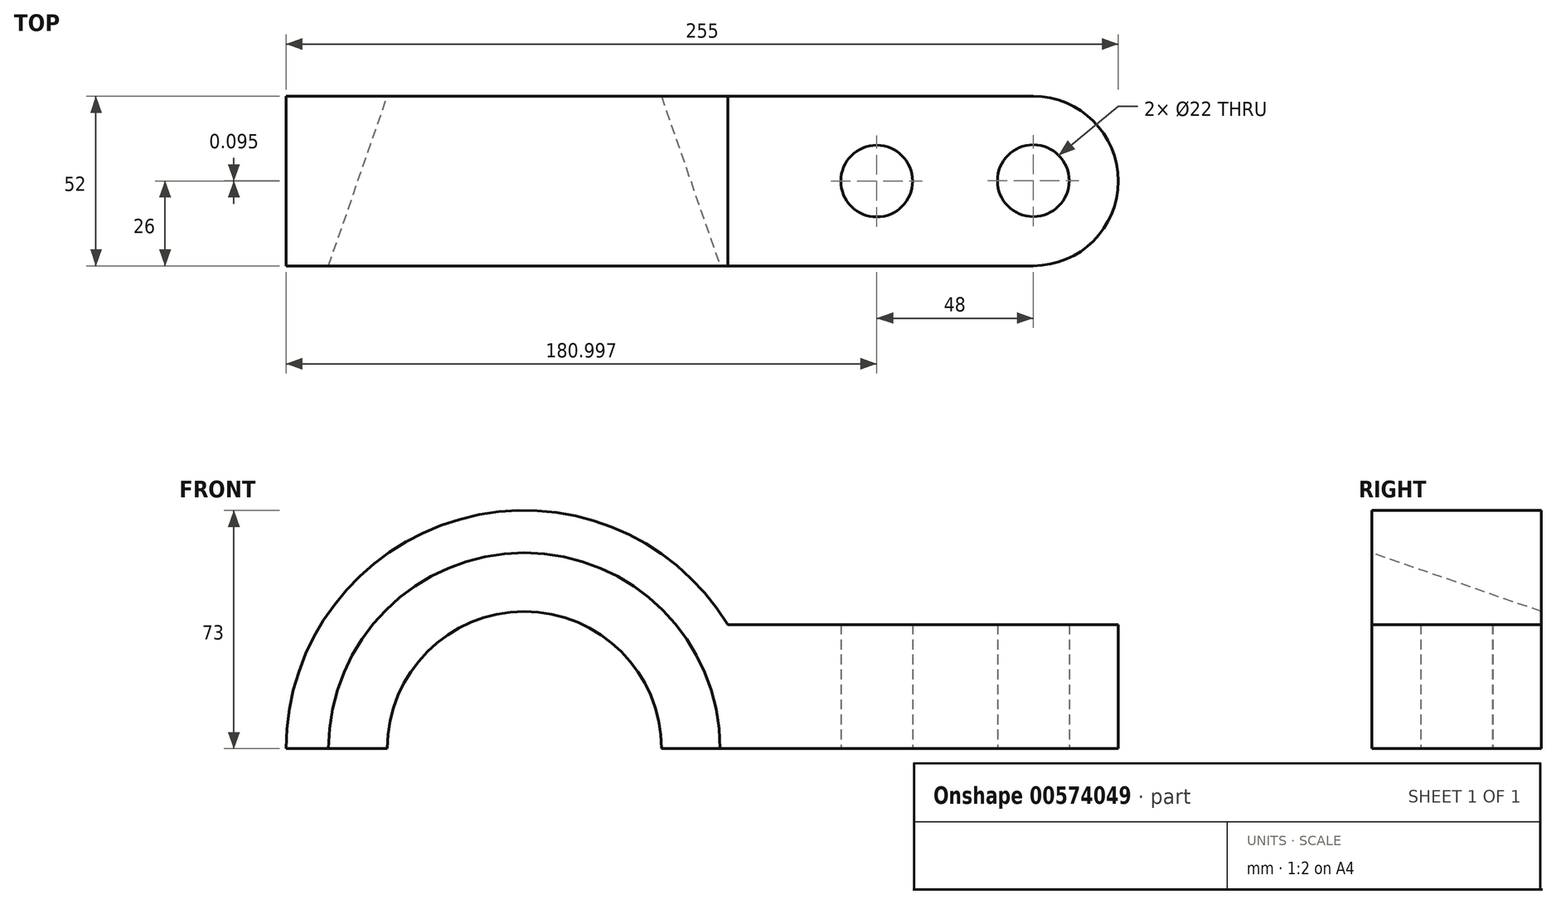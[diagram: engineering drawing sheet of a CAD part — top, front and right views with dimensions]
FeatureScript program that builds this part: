
annotation { "Feature Type Name" : "Feature", "Feature Type Description" : "" }
export const myFeature = defineFeature(function(context is Context, id is Id, definition is map)
    precondition{}
    {
        {
            var Q0;
            Q0=qCreatedBy(makeId("Front.planeOp"),FACE);
            var sketch = newSketch(context, id + "F0", { "sketchPlane" : qUnion([Q0])});
            skArc(sketch, "E0", {"start": v(-38.55, 38) * mm, "mid": v(-120.62, 70.28) * mm, "end": v(-173.88, 0) * mm});
            skArc(sketch, "E1", {"start": v(-40.88, 0) * mm, "mid": v(-100.88, 60) * mm, "end": v(-160.88, 0) * mm});
            skArc(sketch, "E2", {"start": v(-58.88, 0) * mm, "mid": v(-100.88, 42) * mm, "end": v(-142.88, 0) * mm});
            skLineSegment(sketch, "E3", {"start": v(-38.55, 38) * mm, "end": v(81.12, 38) * mm});
            skLineSegment(sketch, "E4", {"start": v(81.12, 38) * mm, "end": v(81.12, 0) * mm});
            skLineSegment(sketch, "E5", {"start": v(81.12, 0) * mm, "end": v(-27.88, 0) * mm});
            skLineSegment(sketch, "E6", {"start": v(-27.88, 0) * mm, "end": v(-58.88, 0) * mm});
            skLineSegment(sketch, "E7.trimOffspring", {"start": v(-142.88, 0) * mm, "end": v(-173.88, 0) * mm});
            skSolve(sketch);
        }
        {
            var Q0;
            {var subQ1=sQuery(id+"F0.wireOp",EDGE,"E0");Q0=makeQuery(id+"F0.imprint","IMPRINT",FACE,{"disambiguationData":[TD([[makeQuery(id+"F0.imprint","IMPRINT",EDGE,{"derivedFrom":subQ1}),1.0]])]});}
            extrude(context, id + "F1", {"entities" : qUnion([Q0]), "depth" : 52 * mm, "offsetDistance" : 25 * mm});
        }
        {
            var Q0;
            {var subQ0=sQuery(id+"F0.wireOp",EDGE,"E1");Q0=makeQuery(id+"F0.imprint","IMPRINT",FACE,{"disambiguationData":[TD([[makeQuery(id+"F0.imprint","IMPRINT",EDGE,{"derivedFrom":subQ0}),1.0]])]});}
            extrude(context, id + "F2", {"entities" : qUnion([Q0]), "operationType" : NewBodyOperationType.ADD, "depth" : 52 * mm, "offsetDistance" : 25 * mm});
        }
        {
            var Q0;
            {var subQ0=sQuery(id+"F0.wireOp",EDGE,"E7.trimOffspring");Q0=makeQuery(id+"F2.boolean.opBoolean","MERGE",FACE,{"derivedFrom":[makeQuery(id+"F1.opExtrude","SWEPT_FACE",FACE,{"disambiguationData":[OSD([subQ0])]}),makeQuery(id+"F2.opExtrude","SWEPT_FACE",FACE,{"disambiguationData":[OSD([subQ0])]})]});}
            var sketch = newSketch(context, id + "F3", { "sketchPlane" : qUnion([Q0])});
            skLineSegment(sketch, "E8", {"start": v(-100.88, 0) * mm, "end": v(-100.88, 63.58) * mm});
            skLineSegment(sketch, "E9", {"start": v(-142.88, 0) * mm, "end": v(-160.88, 52) * mm});
            skSolve(sketch);
        }
        {
            var Q0;
            {var subQ0=sQuery(id+"F3.wireOp",EDGE,"E9");Q0=makeQuery(id+"F3.imprint","IMPRINT",FACE,{"disambiguationData":[TD([[makeQuery(id+"F3.imprint","IMPRINT",EDGE,{"derivedFrom":subQ0}),-1.0]])]});}
            var Q1;
            Q1=sQuery(id+"F3.wireOp",EDGE,"E8");
            revolve(context, id + "F4", {"operationType" : NewBodyOperationType.REMOVE, "entities" : qUnion([Q0]), "axis" : qUnion([Q1]), "revolveType" : RevolveType.FULL, "oppositeDirection" : true});
        }
        {
            var Q0;
            {var subQ0=sQuery(id+"F0.wireOp",EDGE,"E6");Q0=makeQuery(id+"F2.boolean.opBoolean","MERGE",FACE,{"derivedFrom":[makeQuery(id+"F1.opExtrude","SWEPT_FACE",FACE,{"disambiguationData":[OSD([sQuery(id+"F0.wireOp",EDGE,"E5"),subQ0])]}),makeQuery(id+"F2.opExtrude","SWEPT_FACE",FACE,{"disambiguationData":[OSD([subQ0])]})]});}
            var sketch = newSketch(context, id + "F5", { "sketchPlane" : qUnion([Q0])});
            skCircle(sketch, "E10", {"center": v(7.12, 26) * mm, "radius": 11 * mm});
            skCircle(sketch, "E11", {"center": v(55.12, 25.9) * mm, "radius": 11 * mm});
            skPoint(sketch, "E12.first.point", {"position": v(56.67, 52) * mm});
            skPoint(sketch, "E12.second.point", {"position": v(81.12, 26) * mm});
            skPoint(sketch, "E12.third.point", {"position": v(58.54, 0) * mm});
            skSolve(sketch);
        }
        {
            var Q0;
            Q0=makeQuery(id+"F5.imprint","IMPRINT",FACE,{"disambiguationData":[TD([[makeQuery(id+"F5.imprint","IMPRINT",EDGE,{"derivedFrom":sQuery(id+"F5.wireOp",EDGE,"E10")}),1.0]])]});
            var Q1;
            Q1=makeQuery(id+"F5.imprint","IMPRINT",FACE,{"disambiguationData":[TD([[makeQuery(id+"F5.imprint","IMPRINT",EDGE,{"derivedFrom":sQuery(id+"F5.wireOp",EDGE,"E11")}),1.0]])]});
            extrude(context, id + "F6", {"entities" : qUnion([Q0, Q1]), "operationType" : NewBodyOperationType.REMOVE, "oppositeDirection" : true, "depth" : 47.1 * mm, "offsetDistance" : 25 * mm});
        }
        {
            var Q0;
            Q0=makeQuery(id+"F1.opExtrude","CAP_EDGE",EDGE,{"disambiguationData":[OSD([sQuery(id+"F0.wireOp",EDGE,"E4")])],"isStart":false});
            var Q1;
            Q1=makeQuery(id+"F1.opExtrude","CAP_EDGE",EDGE,{"disambiguationData":[OSD([sQuery(id+"F0.wireOp",EDGE,"E4")])],"isStart":true});
            fillet(context, id + "F7", {"entities" : qUnion([Q0, Q1]), "radius" : 26 * mm, "tangentPropagation" : true, "allowEdgeOverflow" : false});
        }
    });
